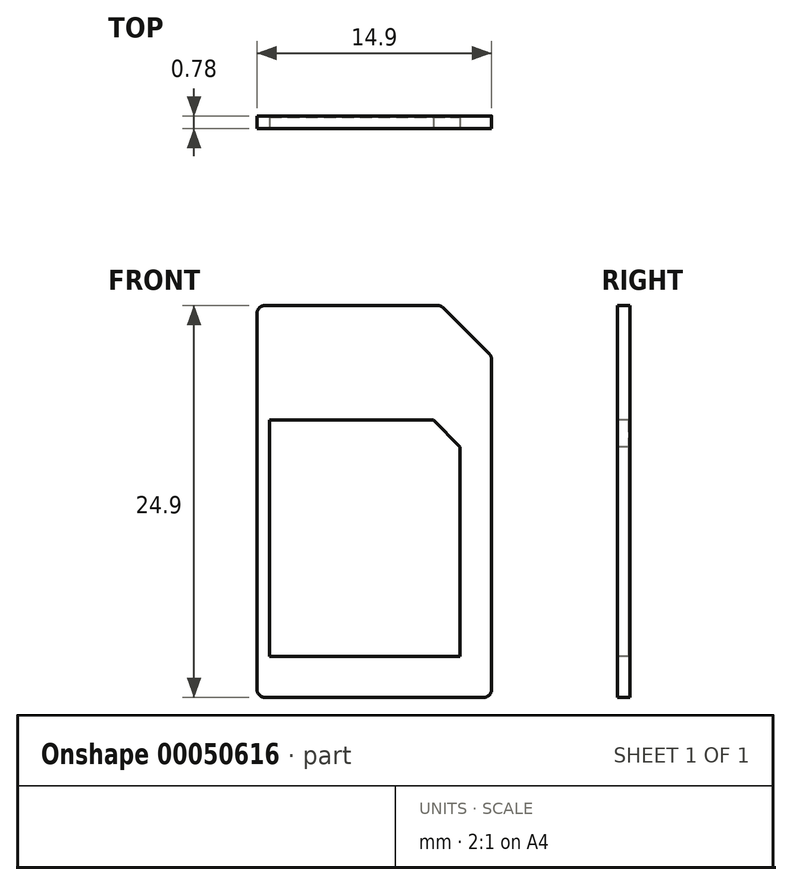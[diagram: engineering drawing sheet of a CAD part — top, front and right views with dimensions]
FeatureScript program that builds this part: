
annotation { "Feature Type Name" : "Feature", "Feature Type Description" : "" }
export const myFeature = defineFeature(function(context is Context, id is Id, definition is map)
    precondition{}
    {
        {
            var Q0;
            Q0=qCreatedBy(makeId("Front.planeOp"),FACE);
            var sketch = newSketch(context, id + "F0", { "sketchPlane" : qUnion([Q0])});
            skLineSegment(sketch, "E0.rect.bottom", {"start": v(-7.45, 12.45) * mm, "end": v(4.22, 12.45) * mm});
            skLineSegment(sketch, "E0.rect.top", {"start": v(-7.45, -12.45) * mm, "end": v(7.45, -12.45) * mm});
            skLineSegment(sketch, "E0.rect.left", {"start": v(-7.45, 12.45) * mm, "end": v(-7.45, -12.45) * mm});
            skLineSegment(sketch, "E0.rect.right", {"start": v(7.45, 9.22) * mm, "end": v(7.45, -12.45) * mm});
            skPoint(sketch, "E0.rect.middle", {"position": v(0, 0) * mm});
            skLineSegment(sketch, "E1", {"start": v(4.22, 12.45) * mm, "end": v(7.45, 9.22) * mm});
            skPoint(sketch, "E2.orphan", {"position": v(7.45, 12.45) * mm});
            skSolve(sketch);
        }
        {
            var Q0;
            Q0=makeQuery(id+"F0.imprint","IMPRINT",FACE,{"disambiguationData":[TD([[makeQuery(id+"F0.imprint","IMPRINT",EDGE,{"derivedFrom":sQuery(id+"F0.wireOp",EDGE,"E0.rect.bottom")}),-1.0]])]});
            extrude(context, id + "F1", {"entities" : qUnion([Q0]), "depth" : 0.78 * mm});
        }
        {
            var Q0;
            Q0=makeQuery(id+"F1.opExtrude","SWEPT_EDGE",EDGE,{"disambiguationData":[OSD([sQuery(id+"F0.wireOp",EDGE,"E0.rect.bottom"),sQuery(id+"F0.wireOp",EDGE,"E0.rect.left")])]});
            var Q1;
            Q1=makeQuery(id+"F1.opExtrude","SWEPT_EDGE",EDGE,{"disambiguationData":[OSD([sQuery(id+"F0.wireOp",EDGE,"E0.rect.top"),sQuery(id+"F0.wireOp",EDGE,"E0.rect.left")])]});
            var Q2;
            Q2=makeQuery(id+"F1.opExtrude","SWEPT_EDGE",EDGE,{"disambiguationData":[OSD([sQuery(id+"F0.wireOp",EDGE,"E0.rect.top"),sQuery(id+"F0.wireOp",EDGE,"E0.rect.right")])]});
            var Q3;
            Q3=makeQuery(id+"F1.opExtrude","SWEPT_EDGE",EDGE,{"disambiguationData":[OSD([sQuery(id+"F0.wireOp",EDGE,"E0.rect.bottom"),sQuery(id+"F0.wireOp",EDGE,"E0.rect.right")])]});
            fillet(context, id + "F2", {"entities" : qUnion([Q0, Q1, Q2, Q3]), "radius" : 0.5 * mm, "tangentPropagation" : true, "allowEdgeOverflow" : false});
        }
        {
            var Q0;
            Q0=makeQuery(id+"F1.opExtrude","CAP_FACE",FACE,{"disambiguationData":[OSD([sQuery(id+"F0.wireOp",EDGE,"E0.rect.bottom"),sQuery(id+"F0.wireOp",EDGE,"E0.rect.top"),sQuery(id+"F0.wireOp",EDGE,"E0.rect.left"),sQuery(id+"F0.wireOp",EDGE,"E0.rect.right"),sQuery(id+"F0.wireOp",EDGE,"E1")])],"isStart":false});
            var sketch = newSketch(context, id + "F3", { "sketchPlane" : qUnion([Q0])});
            skLineSegment(sketch, "E3.bottom", {"start": v(-6.65, 5.17) * mm, "end": v(3.75, 5.17) * mm});
            skLineSegment(sketch, "E3.top", {"start": v(-6.65, -9.83) * mm, "end": v(5.45, -9.83) * mm});
            skLineSegment(sketch, "E3.left", {"start": v(-6.65, 5.17) * mm, "end": v(-6.65, -9.83) * mm});
            skLineSegment(sketch, "E3.right", {"start": v(5.45, 3.47) * mm, "end": v(5.45, -9.83) * mm});
            skLineSegment(sketch, "E4", {"start": v(-7.45, -5.49) * mm, "end": v(-6.65, -5.49) * mm, "construction": true});
            skLineSegment(sketch, "E5", {"start": v(0, -9.83) * mm, "end": v(0, -12.45) * mm, "construction": true});
            skLineSegment(sketch, "E6", {"start": v(3.75, 5.17) * mm, "end": v(5.45, 3.47) * mm});
            skSolve(sketch);
        }
        {
            var Q0;
            Q0=makeQuery(id+"F3.imprint","IMPRINT",FACE,{"disambiguationData":[TD([[makeQuery(id+"F3.imprint","IMPRINT",EDGE,{"derivedFrom":sQuery(id+"F3.wireOp",EDGE,"E3.bottom")}),-1.0]])]});
            extrude(context, id + "F4", {"entities" : qUnion([Q0]), "operationType" : NewBodyOperationType.REMOVE, "oppositeDirection" : true, "depth" : 0.7 * mm});
        }
    });
